# Revit family: NBS_Allermuir_OffcChrs-en-us-Obris_2SeatSofa
name_source: partatom
category: Furniture
revit_build: Autodesk Revit 2018 (Build: 20190510_1515(x64)
units: mm (PartAtom-declared; Revit-internal decimal feet)

## family parameters
Always vertical = Yes
Cut with Voids When Loaded = No
Room Calculation Point = No
Shared = No
Work Plane-Based = No

## types (1)
- Obris_2SeatSofa_OBR02
    ArmHeight = 30.25"
    AssetType = Movable
    BIMObjectName = NBS_Allermuir_DomesticChairs_Obris_OBR02-US
    Category = Pr_40_50_12_81:Sofas
    Description = Two seat sofa
    DurationUnit = year
    ExpectedLife = 10
    Features = Tubular Steel back frame with foam overmould and tensioned fabric, Tradtional carcass seat with dual density seat foam, Foam core with feather and down back and arm cushions, Solid Beech feet with a Black color wash finish, Reversable plastic/felt glides
    FeetMaterial = NBS_Allermuir_Beech_Black
    Finish = Fabric
    IfcExportAs = IfcFurnitureType
    IfcExportType = SOFA
    IsBuiltIn = No
    ManufacturerName = Allermuir
    ManufacturerURL = www.allermuir.com
    Material = Fabric, Nylon 6, PU foam, Plywood, Aluminium Casting, Aluminium Extrusion, Steel
    ModelNumber = OBR02
    ModelReference = Obris
    NBSCertification = www.nationalbimlibrary.com/cert/jpgt3oy3
    NBSDescription = Domestic Chairs
    NBSReference = 45-35-20/365
    Name = DomesticChairs_OBR02_Obris_Allermuir
    NominalDepth = 36 "
    NominalHeight = 30 "
    NominalLength = 75 "
    NominalWidth = 75 "
    OmniClassCode = 22-12 52 23
    OmniClassTitle = Office Seating
    OmniClassVersion = Table 22 2012-05-16
    ProductInformation = https://www.allermuir.com
    SeatDepth = 31.50"
    SeatHeight = 16.25"
    SeatMaterial = NBS_Allermuir_Fabric
    SeatWidth = 66.50"
    Size = 35.5 x 30.25 x 74.75"
    Status = UNSET
    Style = Sofa
    SustainabilityPerformance = 99% recyclable
    Uniclass2015Code = Pr_40_50_12_81
    Uniclass2015Title = Sofas
    Uniclass2015Version = Products v1.15
    Version = 1
    WarrantyDescription = Allermuir warrant that its manufactured products are free from manufacturing defects - in materials or workmanship - for a period of ten (10) years. , Allermuir will repair, or replace (at Allermuir's sole discretion) with comparable free of charge materials / components, any product / component which fails under normal use in a single shift environment, as a result of a defect in the materials and/ or workmanship
    WarrantyDurationParts = 10
    WarrantyDurationUnit = year

## geometry (parser evidence)
native form markers: Extrusion x3, Sweep x2
no freeform markers — native parametric forms only
